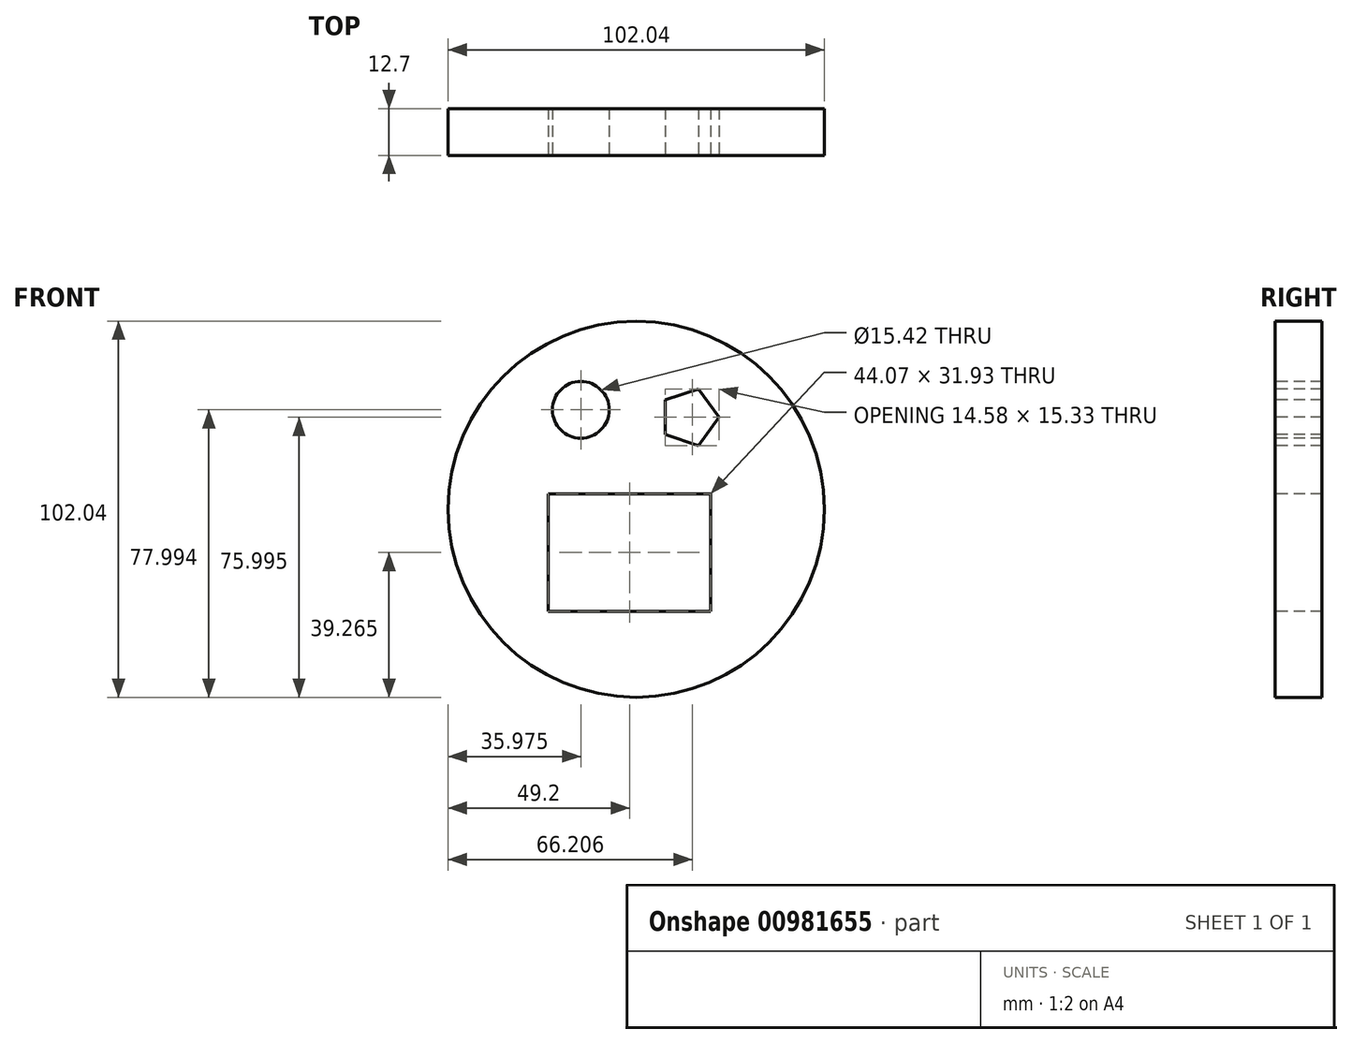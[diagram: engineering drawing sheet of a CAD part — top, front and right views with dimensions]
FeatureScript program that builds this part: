
annotation { "Feature Type Name" : "Feature", "Feature Type Description" : "" }
export const myFeature = defineFeature(function(context is Context, id is Id, definition is map)
    precondition{}
    {
        {
            var Q0;
            Q0=qCreatedBy(makeId("Front.planeOp"),FACE);
            var sketch = newSketch(context, id + "F0", { "sketchPlane" : qUnion([Q0])});
            skCircle(sketch, "E0", {"center": v(-179.41, 27.72) * mm, "radius": 51.02 * mm});
            skSolve(sketch);
        }
        {
            var Q0;
            Q0 = qSketchRegion(id + "F0", true);
            extrude(context, id + "F1", {"entities" : qUnion([Q0]), "depth" : 12.7 * mm, "offsetDistance" : 25.4 * mm});
        }
        {
            var Q0;
            Q0=makeQuery(id+"F1.opExtrude","CAP_FACE",FACE,{"disambiguationData":[OSD([sQuery(id+"F0.wireOp",EDGE,"E0")])],"isStart":false});
            var sketch = newSketch(context, id + "F2", { "sketchPlane" : qUnion([Q0])});
            skLineSegment(sketch, "E1.bottom", {"start": v(-203.26, 31.93) * mm, "end": v(-159.2, 31.93) * mm});
            skLineSegment(sketch, "E1.top", {"start": v(-203.26, 0) * mm, "end": v(-159.2, 0) * mm});
            skLineSegment(sketch, "E1.left", {"start": v(-203.26, 31.93) * mm, "end": v(-203.26, 0) * mm});
            skLineSegment(sketch, "E1.right", {"start": v(-159.2, 31.93) * mm, "end": v(-159.2, 0) * mm});
            skSolve(sketch);
        }
        {
            var Q0;
            Q0 = qSketchRegion(id + "F2", true);
            extrude(context, id + "F3", {"entities" : qUnion([Q0]), "operationType" : NewBodyOperationType.REMOVE, "oppositeDirection" : true, "depth" : 25.4 * mm, "offsetDistance" : 25.4 * mm});
        }
        {
            var Q0;
            Q0=makeQuery(id+"F1.opExtrude","CAP_FACE",FACE,{"disambiguationData":[OSD([sQuery(id+"F0.wireOp",EDGE,"E0")])],"isStart":false});
            var sketch = newSketch(context, id + "F4", { "sketchPlane" : qUnion([Q0])});
            skCircle(sketch, "E2.cCircle", {"center": v(-203.67, 55.54) * mm, "radius": 5.58 * mm, "construction": true});
            skLineSegment(sketch, "E2.0", {"start": v(-197.02, 53.7) * mm, "end": v(-203.36, 48.65) * mm});
            skLineSegment(sketch, "E2.1", {"start": v(-203.36, 48.65) * mm, "end": v(-210.12, 53.12) * mm});
            skLineSegment(sketch, "E2.2", {"start": v(-210.12, 53.12) * mm, "end": v(-207.97, 60.93) * mm});
            skLineSegment(sketch, "E2.3", {"start": v(-207.97, 60.93) * mm, "end": v(-199.87, 61.3) * mm});
            skLineSegment(sketch, "E2.4", {"start": v(-199.87, 61.3) * mm, "end": v(-197.02, 53.7) * mm});
            skPoint(sketch, "E2.0.midPoint", {"position": v(-200.2, 51.18) * mm});
            skCircle(sketch, "E3.cCircle", {"center": v(-165, 52.7) * mm, "radius": 6.52 * mm, "construction": true});
            skLineSegment(sketch, "E3.0", {"start": v(-171.51, 47.96) * mm, "end": v(-171.51, 57.43) * mm});
            skLineSegment(sketch, "E3.1", {"start": v(-171.51, 57.43) * mm, "end": v(-162.5, 60.36) * mm});
            skLineSegment(sketch, "E3.2", {"start": v(-162.5, 60.36) * mm, "end": v(-156.94, 52.7) * mm});
            skLineSegment(sketch, "E3.3", {"start": v(-156.94, 52.7) * mm, "end": v(-162.5, 45.03) * mm});
            skLineSegment(sketch, "E3.4", {"start": v(-162.5, 45.03) * mm, "end": v(-171.51, 47.96) * mm});
            skPoint(sketch, "E3.0.midPoint", {"position": v(-171.51, 52.7) * mm});
            skSolve(sketch);
        }
        {
            var Q0;
            Q0=makeQuery(id+"F4.imprint","IMPRINT",FACE,{"disambiguationData":[TD([[makeQuery(id+"F4.imprint","IMPRINT",EDGE,{"derivedFrom":sQuery(id+"F4.wireOp",EDGE,"E3.0")}),-1.0]])]});
            extrude(context, id + "F5", {"entities" : qUnion([Q0]), "operationType" : NewBodyOperationType.REMOVE, "oppositeDirection" : true, "depth" : 25.4 * mm, "offsetDistance" : 25.4 * mm});
        }
        {
            var Q0;
            Q0=makeQuery(id+"F1.opExtrude","CAP_FACE",FACE,{"disambiguationData":[OSD([sQuery(id+"F0.wireOp",EDGE,"E0")])],"isStart":false});
            var sketch = newSketch(context, id + "F6", { "sketchPlane" : qUnion([Q0])});
            skCircle(sketch, "E4", {"center": v(-194.46, 54.7) * mm, "radius": 7.71 * mm});
            skSolve(sketch);
        }
        {
            var Q0;
            Q0=makeQuery(id+"F6.imprint","IMPRINT",FACE,{"disambiguationData":[TD([[makeQuery(id+"F6.imprint","IMPRINT",EDGE,{"derivedFrom":sQuery(id+"F6.wireOp",EDGE,"E4")}),1.0]])]});
            extrude(context, id + "F7", {"entities" : qUnion([Q0]), "operationType" : NewBodyOperationType.REMOVE, "oppositeDirection" : true, "depth" : 25.4 * mm, "offsetDistance" : 25.4 * mm});
        }
    });
